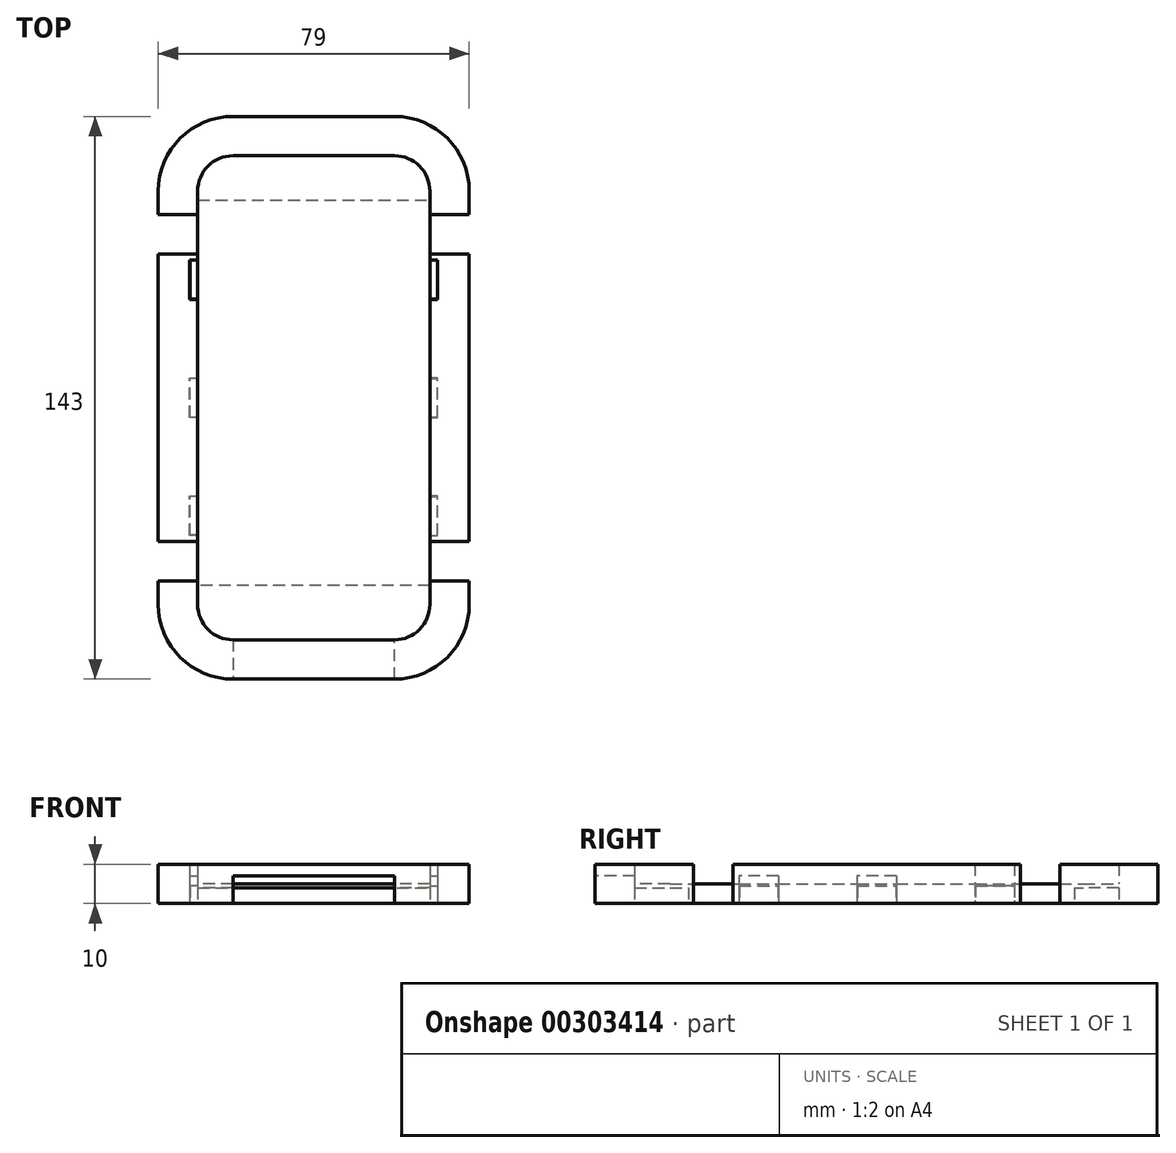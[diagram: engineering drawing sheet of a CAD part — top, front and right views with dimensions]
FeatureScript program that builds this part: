
annotation { "Feature Type Name" : "Feature", "Feature Type Description" : "" }
export const myFeature = defineFeature(function(context is Context, id is Id, definition is map)
    precondition{}
    {
        {
            var Q0;
            Q0=qCreatedBy(makeId("Top.planeOp"),FACE);
            var sketch = newSketch(context, id + "F0", { "sketchPlane" : qUnion([Q0])});
            skLineSegment(sketch, "E0.rect.bottom", {"start": v(20.5, -61.5) * mm, "end": v(-20.5, -61.5) * mm});
            skLineSegment(sketch, "E0.rect.top", {"start": v(20.5, 61.5) * mm, "end": v(-20.5, 61.5) * mm});
            skLineSegment(sketch, "E0.rect.left", {"start": v(29.5, -52.5) * mm, "end": v(29.5, 52.5) * mm});
            skLineSegment(sketch, "E0.rect.right", {"start": v(-29.5, -52.5) * mm, "end": v(-29.5, 52.5) * mm});
            skPoint(sketch, "E0.rect.middle", {"position": v(0, 0) * mm});
            skPoint(sketch, "E1.visualSharp", {"position": v(-29.5, 61.5) * mm});
            skArc(sketch, "E1.filletArc", {"start": v(-20.5, 61.5) * mm, "mid": v(-26.86, 58.86) * mm, "end": v(-29.5, 52.5) * mm});
            skPoint(sketch, "E2.visualSharp", {"position": v(29.5, 61.5) * mm});
            skArc(sketch, "E2.filletArc", {"start": v(29.5, 52.5) * mm, "mid": v(26.86, 58.86) * mm, "end": v(20.5, 61.5) * mm});
            skPoint(sketch, "E3.visualSharp", {"position": v(29.5, -61.5) * mm});
            skArc(sketch, "E3.filletArc", {"start": v(20.5, -61.5) * mm, "mid": v(26.86, -58.86) * mm, "end": v(29.5, -52.5) * mm});
            skPoint(sketch, "E4.visualSharp", {"position": v(-29.5, -61.5) * mm});
            skArc(sketch, "E4.filletArc", {"start": v(-29.5, -52.5) * mm, "mid": v(-26.86, -58.86) * mm, "end": v(-20.5, -61.5) * mm});
            skSolve(sketch);
        }
        {
            var Q0;
            Q0=makeQuery(id+"F0.imprint","IMPRINT",FACE,{"disambiguationData":[TD([[makeQuery(id+"F0.imprint","IMPRINT",EDGE,{"derivedFrom":sQuery(id+"F0.wireOp",EDGE,"E0.rect.bottom")}),-1.0]])]});
            extrude(context, id + "F1", {"entities" : qUnion([Q0]), "oppositeDirection" : true, "depth" : 1 * mm});
        }
        {
            var Q0;
            Q0=makeQuery(id+"F0.imprint","IMPRINT",FACE,{"disambiguationData":[TD([[makeQuery(id+"F0.imprint","IMPRINT",EDGE,{"derivedFrom":sQuery(id+"F0.wireOp",EDGE,"E0.rect.bottom")}),-1.0]])]});
            var sketch = newSketch(context, id + "F2", { "sketchPlane" : qUnion([Q0])});
            skLineSegment(sketch, "E5.0", {"start": v(-39.5, -52.5) * mm, "end": v(-39.5, 52.5) * mm});
            skArc(sketch, "E5.1", {"start": v(-20.5, 71.5) * mm, "mid": v(-33.94, 65.94) * mm, "end": v(-39.5, 52.5) * mm});
            skArc(sketch, "E5.2", {"start": v(-39.5, -52.5) * mm, "mid": v(-33.94, -65.94) * mm, "end": v(-20.5, -71.5) * mm});
            skLineSegment(sketch, "E5.3", {"start": v(20.5, 71.5) * mm, "end": v(-20.5, 71.5) * mm});
            skLineSegment(sketch, "E5.4", {"start": v(20.5, -71.5) * mm, "end": v(-20.5, -71.5) * mm});
            skArc(sketch, "E5.5", {"start": v(20.5, -71.5) * mm, "mid": v(33.94, -65.94) * mm, "end": v(39.5, -52.5) * mm});
            skLineSegment(sketch, "E5.6", {"start": v(39.5, -52.5) * mm, "end": v(39.5, 52.5) * mm});
            skArc(sketch, "E5.7", {"start": v(39.5, 52.5) * mm, "mid": v(33.94, 65.94) * mm, "end": v(20.5, 71.5) * mm});
            skLineSegment(sketch, "E6", {"start": v(0, -46.5) * mm, "end": v(39.5, -46.5) * mm});
            skLineSegment(sketch, "E7", {"start": v(39.5, -46.5) * mm, "end": v(39.5, -36.5) * mm});
            skLineSegment(sketch, "E8", {"start": v(39.5, -36.5) * mm, "end": v(-39.5, -36.5) * mm});
            skLineSegment(sketch, "E9", {"start": v(-39.5, -36.5) * mm, "end": v(-39.5, -46.5) * mm});
            skLineSegment(sketch, "E10", {"start": v(-39.5, -46.5) * mm, "end": v(0, -46.5) * mm});
            skLineSegment(sketch, "E11", {"start": v(0, 46.5) * mm, "end": v(39.5, 46.5) * mm});
            skLineSegment(sketch, "E12", {"start": v(39.5, 46.5) * mm, "end": v(39.5, 36.5) * mm});
            skLineSegment(sketch, "E13", {"start": v(39.5, 36.5) * mm, "end": v(-39.5, 36.5) * mm});
            skLineSegment(sketch, "E14", {"start": v(-39.5, 36.5) * mm, "end": v(-39.5, 46.5) * mm});
            skLineSegment(sketch, "E15", {"start": v(-39.5, 46.5) * mm, "end": v(0, 46.5) * mm});
            skLineSegment(sketch, "E16.bottom", {"start": v(5, -36.5) * mm, "end": v(-5, -36.5) * mm});
            skLineSegment(sketch, "E16.top", {"start": v(5, 36.5) * mm, "end": v(-5, 36.5) * mm});
            skLineSegment(sketch, "E16.left", {"start": v(5, -36.5) * mm, "end": v(5, 36.5) * mm});
            skLineSegment(sketch, "E16.right", {"start": v(-5, -36.5) * mm, "end": v(-5, 36.5) * mm});
            skPoint(sketch, "E16.middle", {"position": v(0, 0) * mm});
            skSolve(sketch);
        }
        {
            var Q0;
            {var subQ12=sQuery(id+"F2.wireOp",EDGE,"E5.2");Q0=makeQuery(id+"F2.imprint","IMPRINT",FACE,{"disambiguationData":[TD([[makeQuery(id+"F2.imprint","IMPRINT",EDGE,{"derivedFrom":subQ12}),1.0]])]});}
            var Q1;
            {var subQ0=sQuery(id+"F2.wireOp",EDGE,"E9");Q1=makeQuery(id+"F2.imprint","IMPRINT",FACE,{"disambiguationData":[TD([[makeQuery(id+"F2.imprint","IMPRINT",EDGE,{"derivedFrom":subQ0}),1.0]])]});}
            var Q2;
            {var subQ0=sQuery(id+"F2.wireOp",EDGE,"E7");Q2=makeQuery(id+"F2.imprint","IMPRINT",FACE,{"disambiguationData":[TD([[makeQuery(id+"F2.imprint","IMPRINT",EDGE,{"derivedFrom":subQ0}),1.0]])]});}
            var Q3;
            {var subQ0=sQuery(id+"F2.wireOp",EDGE,"E8");var subQ5=makeQuery(id+"F0.imprint","IMPRINT",EDGE,{"derivedFrom":sQuery(id+"F0.wireOp",EDGE,"E0.rect.left")});var subQ6=makeQuery(id+"F2.imprint","INTERSECT",VERTEX,{"derivedFrom":[subQ5,subQ0]});Q3=makeQuery(id+"F2.imprint","IMPRINT",FACE,{"disambiguationData":[TD([[makeQuery(id+"F2.imprint","IMPRINT",EDGE,{"disambiguationData":[TD([[subQ6,-1.0]])],"derivedFrom":subQ5}),-1.0]])]});}
            var Q4;
            {var subQ0=sQuery(id+"F2.wireOp",EDGE,"E12");Q4=makeQuery(id+"F2.imprint","IMPRINT",FACE,{"disambiguationData":[TD([[makeQuery(id+"F2.imprint","IMPRINT",EDGE,{"derivedFrom":subQ0}),-1.0]])]});}
            var Q5;
            {var subQ0=sQuery(id+"F2.wireOp",EDGE,"E14");Q5=makeQuery(id+"F2.imprint","IMPRINT",FACE,{"disambiguationData":[TD([[makeQuery(id+"F2.imprint","IMPRINT",EDGE,{"derivedFrom":subQ0}),-1.0]])]});}
            var Q6;
            {var subQ0=sQuery(id+"F2.wireOp",EDGE,"E8");var subQ5=makeQuery(id+"F0.imprint","IMPRINT",EDGE,{"derivedFrom":sQuery(id+"F0.wireOp",EDGE,"E0.rect.right")});var subQ6=makeQuery(id+"F2.imprint","INTERSECT",VERTEX,{"derivedFrom":[subQ5,subQ0]});Q6=makeQuery(id+"F2.imprint","IMPRINT",FACE,{"disambiguationData":[TD([[makeQuery(id+"F2.imprint","IMPRINT",EDGE,{"disambiguationData":[TD([[subQ6,-1.0]])],"derivedFrom":subQ5}),1.0]])]});}
            var Q7;
            {var subQ5=sQuery(id+"F2.wireOp",EDGE,"E16.bottom");Q7=makeQuery(id+"F2.imprint","IMPRINT",FACE,{"disambiguationData":[TD([[makeQuery(id+"F2.imprint","IMPRINT",EDGE,{"derivedFrom":subQ5}),1.0]])]});}
            var Q8;
            Q8=makeQuery(id+"F2.imprint","IMPRINT",FACE,{"disambiguationData":[TD([[makeQuery(id+"F2.imprint","IMPRINT",EDGE,{"derivedFrom":sQuery(id+"F2.wireOp",EDGE,"E16.bottom")}),-1.0]])]});
            var Q9;
            {var subQ5=sQuery(id+"F2.wireOp",EDGE,"E16.top");Q9=makeQuery(id+"F2.imprint","IMPRINT",FACE,{"disambiguationData":[TD([[makeQuery(id+"F2.imprint","IMPRINT",EDGE,{"derivedFrom":subQ5}),-1.0]])]});}
            var Q10;
            {var subQ12=sQuery(id+"F2.wireOp",EDGE,"E5.1");Q10=makeQuery(id+"F2.imprint","IMPRINT",FACE,{"disambiguationData":[TD([[makeQuery(id+"F2.imprint","IMPRINT",EDGE,{"derivedFrom":subQ12}),1.0]])]});}
            extrude(context, id + "F3", {"entities" : qUnion([Q0, Q1, Q2, Q3, Q4, Q5, Q6, Q7, Q8, Q9, Q10]), "depth" : 5 * mm});
        }
        {
            var Q0;
            {var subQ0=sQuery(id+"F2.wireOp",EDGE,"E8");var subQ5=makeQuery(id+"F0.imprint","IMPRINT",EDGE,{"derivedFrom":sQuery(id+"F0.wireOp",EDGE,"E0.rect.right")});var subQ6=makeQuery(id+"F2.imprint","INTERSECT",VERTEX,{"derivedFrom":[subQ5,subQ0]});Q0=makeQuery(id+"F2.imprint","IMPRINT",FACE,{"disambiguationData":[TD([[makeQuery(id+"F2.imprint","IMPRINT",EDGE,{"disambiguationData":[TD([[subQ6,-1.0]])],"derivedFrom":subQ5}),1.0]])]});}
            var Q1;
            {var subQ0=sQuery(id+"F2.wireOp",EDGE,"E9");Q1=makeQuery(id+"F2.imprint","IMPRINT",FACE,{"disambiguationData":[TD([[makeQuery(id+"F2.imprint","IMPRINT",EDGE,{"derivedFrom":subQ0}),1.0]])]});}
            var Q2;
            {var subQ12=sQuery(id+"F2.wireOp",EDGE,"E5.2");Q2=makeQuery(id+"F2.imprint","IMPRINT",FACE,{"disambiguationData":[TD([[makeQuery(id+"F2.imprint","IMPRINT",EDGE,{"derivedFrom":subQ12}),1.0]])]});}
            var Q3;
            {var subQ0=sQuery(id+"F2.wireOp",EDGE,"E14");Q3=makeQuery(id+"F2.imprint","IMPRINT",FACE,{"disambiguationData":[TD([[makeQuery(id+"F2.imprint","IMPRINT",EDGE,{"derivedFrom":subQ0}),-1.0]])]});}
            var Q4;
            {var subQ12=sQuery(id+"F2.wireOp",EDGE,"E5.1");Q4=makeQuery(id+"F2.imprint","IMPRINT",FACE,{"disambiguationData":[TD([[makeQuery(id+"F2.imprint","IMPRINT",EDGE,{"derivedFrom":subQ12}),1.0]])]});}
            var Q5;
            {var subQ0=sQuery(id+"F2.wireOp",EDGE,"E12");Q5=makeQuery(id+"F2.imprint","IMPRINT",FACE,{"disambiguationData":[TD([[makeQuery(id+"F2.imprint","IMPRINT",EDGE,{"derivedFrom":subQ0}),-1.0]])]});}
            var Q6;
            {var subQ0=sQuery(id+"F2.wireOp",EDGE,"E7");Q6=makeQuery(id+"F2.imprint","IMPRINT",FACE,{"disambiguationData":[TD([[makeQuery(id+"F2.imprint","IMPRINT",EDGE,{"derivedFrom":subQ0}),1.0]])]});}
            var Q7;
            {var subQ0=sQuery(id+"F2.wireOp",EDGE,"E8");var subQ5=makeQuery(id+"F0.imprint","IMPRINT",EDGE,{"derivedFrom":sQuery(id+"F0.wireOp",EDGE,"E0.rect.left")});var subQ6=makeQuery(id+"F2.imprint","INTERSECT",VERTEX,{"derivedFrom":[subQ5,subQ0]});Q7=makeQuery(id+"F2.imprint","IMPRINT",FACE,{"disambiguationData":[TD([[makeQuery(id+"F2.imprint","IMPRINT",EDGE,{"disambiguationData":[TD([[subQ6,-1.0]])],"derivedFrom":subQ5}),-1.0]])]});}
            extrude(context, id + "F4", {"entities" : qUnion([Q0, Q1, Q2, Q3, Q4, Q5, Q6, Q7]), "operationType" : NewBodyOperationType.ADD, "oppositeDirection" : true, "depth" : 5 * mm});
        }
        {
            var Q0;
            Q0=makeQuery(id+"F4.opExtrude","CAP_FACE",FACE,{"disambiguationData":[OSD([sQuery(id+"F0.wireOp",EDGE,"E0.rect.bottom"),sQuery(id+"F0.wireOp",EDGE,"E0.rect.top"),sQuery(id+"F0.wireOp",EDGE,"E0.rect.left"),sQuery(id+"F0.wireOp",EDGE,"E0.rect.right"),sQuery(id+"F0.wireOp",EDGE,"E1.filletArc"),sQuery(id+"F0.wireOp",EDGE,"E2.filletArc"),sQuery(id+"F0.wireOp",EDGE,"E3.filletArc"),sQuery(id+"F0.wireOp",EDGE,"E4.filletArc"),sQuery(id+"F2.wireOp",EDGE,"E5.0"),sQuery(id+"F2.wireOp",EDGE,"E5.1"),sQuery(id+"F2.wireOp",EDGE,"E5.2"),sQuery(id+"F2.wireOp",EDGE,"E5.3"),sQuery(id+"F2.wireOp",EDGE,"E5.4"),sQuery(id+"F2.wireOp",EDGE,"E5.5"),sQuery(id+"F2.wireOp",EDGE,"E5.6"),sQuery(id+"F2.wireOp",EDGE,"E5.7"),sQuery(id+"F2.wireOp",EDGE,"E7"),sQuery(id+"F2.wireOp",EDGE,"E9"),sQuery(id+"F2.wireOp",EDGE,"E12"),sQuery(id+"F2.wireOp",EDGE,"E14")])],"isStart":false});
            var sketch = newSketch(context, id + "F5", { "sketchPlane" : qUnion([Q0])});
            skLineSegment(sketch, "E17", {"start": v(0, 0) * mm, "end": v(-29.5, 0) * mm});
            skLineSegment(sketch, "E18", {"start": v(-29.5, 0) * mm, "end": v(0, 0) * mm});
            skLineSegment(sketch, "E19", {"start": v(0, 0) * mm, "end": v(29.5, 0) * mm});
            skLineSegment(sketch, "E20", {"start": v(29.5, 0) * mm, "end": v(29.5, 5) * mm});
            skLineSegment(sketch, "E21", {"start": v(29.5, 5) * mm, "end": v(31.5, 5) * mm});
            skLineSegment(sketch, "E22", {"start": v(31.5, 5) * mm, "end": v(31.5, -5) * mm});
            skLineSegment(sketch, "E23", {"start": v(31.5, -5) * mm, "end": v(29.5, -5) * mm});
            skLineSegment(sketch, "E24", {"start": v(29.5, -5) * mm, "end": v(29.5, 0) * mm});
            skLineSegment(sketch, "E25", {"start": v(-29.5, 0) * mm, "end": v(-29.5, 5) * mm});
            skLineSegment(sketch, "E26", {"start": v(-29.5, 5) * mm, "end": v(-31.5, 5) * mm});
            skLineSegment(sketch, "E27", {"start": v(-31.5, 5) * mm, "end": v(-31.5, -5) * mm});
            skLineSegment(sketch, "E28", {"start": v(-31.5, -5) * mm, "end": v(-29.5, -5) * mm});
            skLineSegment(sketch, "E29", {"start": v(-29.5, -5) * mm, "end": v(-29.5, 0) * mm});
            skLineSegment(sketch, "E30", {"start": v(29.5, 5) * mm, "end": v(29.5, 25) * mm});
            skLineSegment(sketch, "E31", {"start": v(29.5, 25) * mm, "end": v(29.5, 35) * mm});
            skLineSegment(sketch, "E32", {"start": v(29.5, 35) * mm, "end": v(31.5, 35) * mm});
            skLineSegment(sketch, "E33", {"start": v(31.5, 35) * mm, "end": v(31.5, 25) * mm});
            skLineSegment(sketch, "E34", {"start": v(31.5, 25) * mm, "end": v(29.5, 25) * mm});
            skLineSegment(sketch, "E35", {"start": v(29.5, -5) * mm, "end": v(29.5, -25) * mm});
            skLineSegment(sketch, "E36", {"start": v(29.5, -25) * mm, "end": v(31.5, -25) * mm});
            skLineSegment(sketch, "E37", {"start": v(31.5, -25) * mm, "end": v(31.5, -35) * mm});
            skLineSegment(sketch, "E38", {"start": v(31.5, -35) * mm, "end": v(29.5, -35) * mm});
            skLineSegment(sketch, "E39", {"start": v(29.5, -35) * mm, "end": v(29.5, -25) * mm});
            skLineSegment(sketch, "E40", {"start": v(-29.5, -5) * mm, "end": v(-29.5, -25) * mm});
            skLineSegment(sketch, "E41", {"start": v(-29.5, -25) * mm, "end": v(-29.5, -35) * mm});
            skLineSegment(sketch, "E42", {"start": v(-29.5, -35) * mm, "end": v(-31.5, -35) * mm});
            skLineSegment(sketch, "E43", {"start": v(-31.5, -35) * mm, "end": v(-31.5, -25) * mm});
            skLineSegment(sketch, "E44", {"start": v(-31.5, -25) * mm, "end": v(-29.5, -25) * mm});
            skLineSegment(sketch, "E45", {"start": v(-29.5, 5) * mm, "end": v(-29.5, 25) * mm});
            skLineSegment(sketch, "E46", {"start": v(-29.5, 25) * mm, "end": v(-29.5, 35) * mm});
            skLineSegment(sketch, "E47", {"start": v(-29.5, 35) * mm, "end": v(-31.5, 35) * mm});
            skLineSegment(sketch, "E48", {"start": v(-31.5, 35) * mm, "end": v(-31.5, 25) * mm});
            skLineSegment(sketch, "E49", {"start": v(-31.5, 25) * mm, "end": v(-29.5, 25) * mm});
            skLineSegment(sketch, "E50", {"start": v(-20.5, 61.5) * mm, "end": v(-20.5, 71.5) * mm});
            skLineSegment(sketch, "E51", {"start": v(-20.5, 71.5) * mm, "end": v(20.5, 71.5) * mm});
            skLineSegment(sketch, "E52", {"start": v(20.5, 71.5) * mm, "end": v(20.5, 61.5) * mm});
            skLineSegment(sketch, "E53", {"start": v(20.5, 61.5) * mm, "end": v(-20.5, 61.5) * mm});
            skSolve(sketch);
        }
        {
            var Q0;
            Q0=makeQuery(id+"F5.imprint","IMPRINT",FACE,{"disambiguationData":[TD([[makeQuery(id+"F5.imprint","IMPRINT",EDGE,{"derivedFrom":sQuery(id+"F5.wireOp",EDGE,"E46")}),-1.0]])]});
            var Q1;
            Q1=makeQuery(id+"F5.imprint","IMPRINT",FACE,{"disambiguationData":[TD([[makeQuery(id+"F5.imprint","IMPRINT",EDGE,{"derivedFrom":sQuery(id+"F5.wireOp",EDGE,"E25")}),-1.0]])]});
            var Q2;
            Q2=makeQuery(id+"F5.imprint","IMPRINT",FACE,{"disambiguationData":[TD([[makeQuery(id+"F5.imprint","IMPRINT",EDGE,{"derivedFrom":sQuery(id+"F5.wireOp",EDGE,"E41")}),-1.0]])]});
            var Q3;
            Q3=makeQuery(id+"F5.imprint","IMPRINT",FACE,{"disambiguationData":[TD([[makeQuery(id+"F5.imprint","IMPRINT",EDGE,{"derivedFrom":sQuery(id+"F5.wireOp",EDGE,"E36")}),-1.0]])]});
            var Q4;
            Q4=makeQuery(id+"F5.imprint","IMPRINT",FACE,{"disambiguationData":[TD([[makeQuery(id+"F5.imprint","IMPRINT",EDGE,{"derivedFrom":sQuery(id+"F5.wireOp",EDGE,"E20")}),1.0]])]});
            var Q5;
            Q5=makeQuery(id+"F5.imprint","IMPRINT",FACE,{"disambiguationData":[TD([[makeQuery(id+"F5.imprint","IMPRINT",EDGE,{"derivedFrom":sQuery(id+"F5.wireOp",EDGE,"E31")}),1.0]])]});
            extrude(context, id + "F6", {"entities" : qUnion([Q0, Q1, Q2, Q3, Q4, Q5]), "operationType" : NewBodyOperationType.REMOVE, "oppositeDirection" : true, "depth" : 10 * mm});
        }
        {
            var Q0;
            Q0 = qSketchRegion(id + "F5", true);
            extrude(context, id + "F7", {"entities" : qUnion([Q0]), "operationType" : NewBodyOperationType.REMOVE, "oppositeDirection" : true, "depth" : 7 * mm});
        }
        {
            var Q0;
            Q0=makeQuery(id+"F1.opExtrude","CAP_FACE",FACE,{"disambiguationData":[OSD([sQuery(id+"F0.wireOp",EDGE,"E0.rect.bottom"),sQuery(id+"F0.wireOp",EDGE,"E0.rect.top"),sQuery(id+"F0.wireOp",EDGE,"E0.rect.left"),sQuery(id+"F0.wireOp",EDGE,"E0.rect.right"),sQuery(id+"F0.wireOp",EDGE,"E1.filletArc"),sQuery(id+"F0.wireOp",EDGE,"E2.filletArc"),sQuery(id+"F0.wireOp",EDGE,"E3.filletArc"),sQuery(id+"F0.wireOp",EDGE,"E4.filletArc")])],"isStart":false});
            var sketch = newSketch(context, id + "F8", { "sketchPlane" : qUnion([Q0])});
            skLineSegment(sketch, "E54.bottom", {"start": v(27, 47.75) * mm, "end": v(-27, 47.75) * mm});
            skLineSegment(sketch, "E54.top", {"start": v(27, -47.75) * mm, "end": v(-27, -47.75) * mm});
            skLineSegment(sketch, "E54.left", {"start": v(27, 47.75) * mm, "end": v(27, -47.75) * mm});
            skLineSegment(sketch, "E54.right", {"start": v(-27, 47.75) * mm, "end": v(-27, -47.75) * mm});
            skPoint(sketch, "E54.middle", {"position": v(0, 0) * mm});
            skLineSegment(sketch, "E55.0", {"start": v(29.5, 47.75) * mm, "end": v(29.5, -50.25) * mm});
            skLineSegment(sketch, "E55.1", {"start": v(29.5, -50.25) * mm, "end": v(-29.5, -50.25) * mm});
            skLineSegment(sketch, "E55.2", {"start": v(-29.5, 47.75) * mm, "end": v(-29.5, -50.25) * mm});
            skLineSegment(sketch, "E56", {"start": v(-27, 47.75) * mm, "end": v(-29.5, 47.75) * mm});
            skLineSegment(sketch, "E57", {"start": v(29.5, 47.75) * mm, "end": v(27, 47.75) * mm});
            skLineSegment(sketch, "E58.bottom", {"start": v(-29.5, 34.9) * mm, "end": v(-31.4, 34.9) * mm});
            skLineSegment(sketch, "E58.top", {"start": v(-29.5, 25.1) * mm, "end": v(-31.4, 25.1) * mm});
            skLineSegment(sketch, "E58.left", {"start": v(-29.5, 34.9) * mm, "end": v(-29.5, 25.1) * mm});
            skLineSegment(sketch, "E58.right", {"start": v(-31.4, 34.9) * mm, "end": v(-31.4, 25.1) * mm});
            skLineSegment(sketch, "E59.bottom", {"start": v(-29.5, 4.96) * mm, "end": v(-31.42, 4.96) * mm});
            skLineSegment(sketch, "E59.top", {"start": v(-29.5, -4.94) * mm, "end": v(-31.42, -4.94) * mm});
            skLineSegment(sketch, "E59.left", {"start": v(-29.5, 4.96) * mm, "end": v(-29.5, -4.94) * mm});
            skLineSegment(sketch, "E59.right", {"start": v(-31.42, 4.96) * mm, "end": v(-31.42, -4.94) * mm});
            skLineSegment(sketch, "E60.bottom", {"start": v(-29.5, -25.04) * mm, "end": v(-31.49, -25.04) * mm});
            skLineSegment(sketch, "E60.top", {"start": v(-29.5, -34.99) * mm, "end": v(-31.49, -34.99) * mm});
            skLineSegment(sketch, "E60.left", {"start": v(-29.5, -25.04) * mm, "end": v(-29.5, -34.99) * mm});
            skLineSegment(sketch, "E60.right", {"start": v(-31.49, -25.04) * mm, "end": v(-31.49, -34.99) * mm});
            skLineSegment(sketch, "E61.bottom", {"start": v(29.5, 34.93) * mm, "end": v(31.44, 34.93) * mm});
            skLineSegment(sketch, "E61.top", {"start": v(29.5, 25.08) * mm, "end": v(31.44, 25.08) * mm});
            skLineSegment(sketch, "E61.left", {"start": v(29.5, 34.93) * mm, "end": v(29.5, 25.08) * mm});
            skLineSegment(sketch, "E61.right", {"start": v(31.44, 34.93) * mm, "end": v(31.44, 25.08) * mm});
            skLineSegment(sketch, "E62.bottom", {"start": v(29.5, 4.94) * mm, "end": v(31.45, 4.94) * mm});
            skLineSegment(sketch, "E62.top", {"start": v(29.5, -4.94) * mm, "end": v(31.45, -4.94) * mm});
            skLineSegment(sketch, "E62.left", {"start": v(29.5, 4.94) * mm, "end": v(29.5, -4.94) * mm});
            skLineSegment(sketch, "E62.right", {"start": v(31.45, 4.94) * mm, "end": v(31.45, -4.94) * mm});
            skLineSegment(sketch, "E63.bottom", {"start": v(29.5, -25.09) * mm, "end": v(31.48, -25.09) * mm});
            skLineSegment(sketch, "E63.top", {"start": v(29.5, -34.99) * mm, "end": v(31.48, -34.99) * mm});
            skLineSegment(sketch, "E63.left", {"start": v(29.5, -25.09) * mm, "end": v(29.5, -34.99) * mm});
            skLineSegment(sketch, "E63.right", {"start": v(31.48, -25.09) * mm, "end": v(31.48, -34.99) * mm});
            skSolve(sketch);
        }
        {
            var Q0;
            Q0=makeQuery(id+"F8.imprint","IMPRINT",FACE,{"disambiguationData":[TD([[makeQuery(id+"F8.imprint","IMPRINT",EDGE,{"derivedFrom":sQuery(id+"F8.wireOp",EDGE,"E54.top")}),1.0]])]});
            var Q1;
            Q1=makeQuery(id+"F8.imprint","IMPRINT",FACE,{"disambiguationData":[TD([[makeQuery(id+"F8.imprint","IMPRINT",EDGE,{"derivedFrom":sQuery(id+"F8.wireOp",EDGE,"E58.bottom")}),1.0]])]});
            var Q2;
            Q2=makeQuery(id+"F8.imprint","IMPRINT",FACE,{"disambiguationData":[TD([[makeQuery(id+"F8.imprint","IMPRINT",EDGE,{"derivedFrom":sQuery(id+"F8.wireOp",EDGE,"E61.bottom")}),-1.0]])]});
            var Q3;
            Q3=makeQuery(id+"F8.imprint","IMPRINT",FACE,{"disambiguationData":[TD([[makeQuery(id+"F8.imprint","IMPRINT",EDGE,{"derivedFrom":sQuery(id+"F8.wireOp",EDGE,"E59.bottom")}),1.0]])]});
            var Q4;
            Q4=makeQuery(id+"F8.imprint","IMPRINT",FACE,{"disambiguationData":[TD([[makeQuery(id+"F8.imprint","IMPRINT",EDGE,{"derivedFrom":sQuery(id+"F8.wireOp",EDGE,"E60.bottom")}),1.0]])]});
            var Q5;
            Q5=makeQuery(id+"F8.imprint","IMPRINT",FACE,{"disambiguationData":[TD([[makeQuery(id+"F8.imprint","IMPRINT",EDGE,{"derivedFrom":sQuery(id+"F8.wireOp",EDGE,"E63.bottom")}),-1.0]])]});
            var Q6;
            Q6=makeQuery(id+"F8.imprint","IMPRINT",FACE,{"disambiguationData":[TD([[makeQuery(id+"F8.imprint","IMPRINT",EDGE,{"derivedFrom":sQuery(id+"F8.wireOp",EDGE,"E62.bottom")}),-1.0]])]});
            extrude(context, id + "F9", {"entities" : qUnion([Q0, Q1, Q2, Q3, Q4, Q5, Q6]), "oppositeDirection" : true, "depth" : .5 * mm});
        }
        {
            var Q0;
            Q0 = qSketchRegion(id + "F8", true);
            extrude(context, id + "F10", {"entities" : qUnion([Q0]), "operationType" : NewBodyOperationType.ADD, "depth" : 4 * mm});
        }
    });
